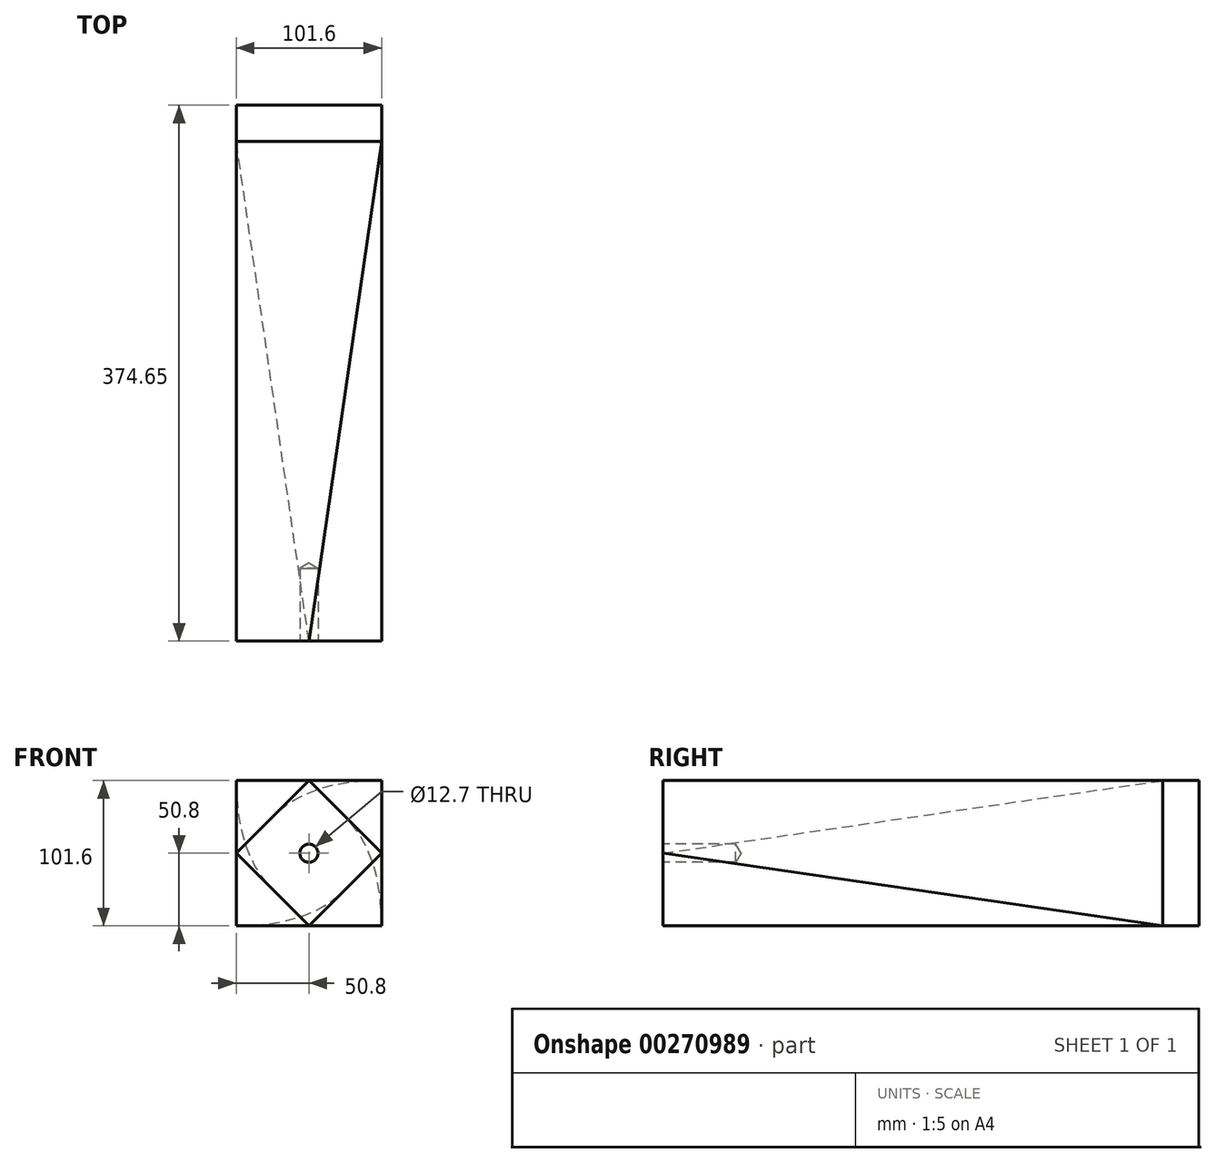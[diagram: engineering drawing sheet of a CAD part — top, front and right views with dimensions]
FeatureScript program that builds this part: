
annotation { "Feature Type Name" : "Feature", "Feature Type Description" : "" }
export const myFeature = defineFeature(function(context is Context, id is Id, definition is map)
    precondition{}
    {
        {
            var Q0;
            Q0=qCreatedBy(makeId("Front.planeOp"),FACE);
            var sketch = newSketch(context, id + "F0", { "sketchPlane" : qUnion([Q0])});
            skLineSegment(sketch, "E0.bottom", {"start": v(0, 0) * mm, "end": v(101.6, 0) * mm});
            skLineSegment(sketch, "E0.top", {"start": v(0, 101.6) * mm, "end": v(101.6, 101.6) * mm});
            skLineSegment(sketch, "E0.left", {"start": v(0, 0) * mm, "end": v(0, 101.6) * mm});
            skLineSegment(sketch, "E0.right", {"start": v(101.6, 0) * mm, "end": v(101.6, 101.6) * mm});
            skSolve(sketch);
        }
        {
            var Q0;
            Q0 = qSketchRegion(id + "F0", true);
            extrude(context, id + "F1", {"entities" : qUnion([Q0]), "depth" : 25.4 * mm});
        }
        {
            var Q0;
            Q0=makeQuery(id+"F1.opExtrude","CAP_FACE",FACE,{"disambiguationData":[OSD([sQuery(id+"F0.wireOp",EDGE,"E0.bottom"),sQuery(id+"F0.wireOp",EDGE,"E0.top"),sQuery(id+"F0.wireOp",EDGE,"E0.left"),sQuery(id+"F0.wireOp",EDGE,"E0.right")])],"isStart":false});
            cPlane(context, id + "F2", {"entities" : qUnion([Q0]), "cplaneType" : CPlaneType.OFFSET, "offset" : 349.25 * mm, "width" : 152.4 * mm, "height" : 152.4 * mm});
        }
        {
            var Q0;
            Q0=qCreatedBy(id+"F2.planeOp",FACE);
            var sketch = newSketch(context, id + "F3", { "sketchPlane" : qUnion([Q0])});
            skLineSegment(sketch, "E1", {"start": v(0, 50.8) * mm, "end": v(50.8, 101.6) * mm});
            skLineSegment(sketch, "E2", {"start": v(50.8, 101.6) * mm, "end": v(101.6, 50.8) * mm});
            skLineSegment(sketch, "E3", {"start": v(101.6, 50.8) * mm, "end": v(50.8, 0) * mm});
            skLineSegment(sketch, "E4", {"start": v(50.8, 0) * mm, "end": v(0, 50.8) * mm});
            skPoint(sketch, "E5.orphan", {"position": v(0, 101.6) * mm});
            skPoint(sketch, "E6.orphan", {"position": v(101.6, 101.6) * mm});
            skPoint(sketch, "E7.orphan", {"position": v(101.6, 0) * mm});
            skPoint(sketch, "E8.left.start.orphan", {"position": v(0, 0) * mm});
            skSolve(sketch);
        }
        {
            var Q1;
            Q1=makeQuery(id+"F3.imprint","IMPRINT",FACE,{"disambiguationData":[TD([[makeQuery(id+"F3.imprint","IMPRINT",EDGE,{"derivedFrom":sQuery(id+"F3.wireOp",EDGE,"E1")}),-1.0]])]});
            var Q2;
            Q2=makeQuery(id+"F1.opExtrude","CAP_FACE",FACE,{"disambiguationData":[OSD([sQuery(id+"F0.wireOp",EDGE,"E0.bottom"),sQuery(id+"F0.wireOp",EDGE,"E0.top"),sQuery(id+"F0.wireOp",EDGE,"E0.left"),sQuery(id+"F0.wireOp",EDGE,"E0.right")])],"isStart":false});
            loft(context, id + "F4", {"operationType" : NewBodyOperationType.ADD, "sheetProfilesArray" : [{ "sheetProfileEntities" : qUnion([Q1]) }, { "sheetProfileEntities" : qUnion([Q2]) }]});
        }
        {
            var Q0;
            Q0=makeQuery(id+"F4.opLoft","CAP_FACE",FACE,{"disambiguationData":[OSD([makeQuery(id+"F3.imprint","IMPRINT",FACE,{"disambiguationData":[TD([[makeQuery(id+"F3.imprint","IMPRINT",EDGE,{"derivedFrom":sQuery(id+"F3.wireOp",EDGE,"E1")}),-1.0]])]})])],"isStart":true});
            var sketch = newSketch(context, id + "F5", { "sketchPlane" : qUnion([Q0])});
            skPoint(sketch, "E9", {"position": v(25.4, 25.4) * mm});
            skPoint(sketch, "E10", {"position": v(50.8, 50.8) * mm});
            skSolve(sketch);
        }
        {
            var Q0;
            Q0=sQuery(id+"F5.wireOp",VERTEX,"E10");
            var Q1;
            Q1=makeQuery(id+"F1.opExtrude","SWEPT_BODY",BODY,{"disambiguationData":[OSD([sQuery(id+"F0.wireOp",EDGE,"E0.bottom"),sQuery(id+"F0.wireOp",EDGE,"E0.top"),sQuery(id+"F0.wireOp",EDGE,"E0.left"),sQuery(id+"F0.wireOp",EDGE,"E0.right")])]});
            hole(context, id + "F6", {"style" : HoleStyle.SIMPLE, "endStyle" : HoleEndStyle.BLIND, "holeDiameter" : 12.7 * mm, "holeDepth" : 50.8 * mm, "tappedDepth" : 12.7 * mm, "tapClearance" : 3, "locations" : qUnion([Q0]), "scope" : qUnion([Q1])});
        }
    });
